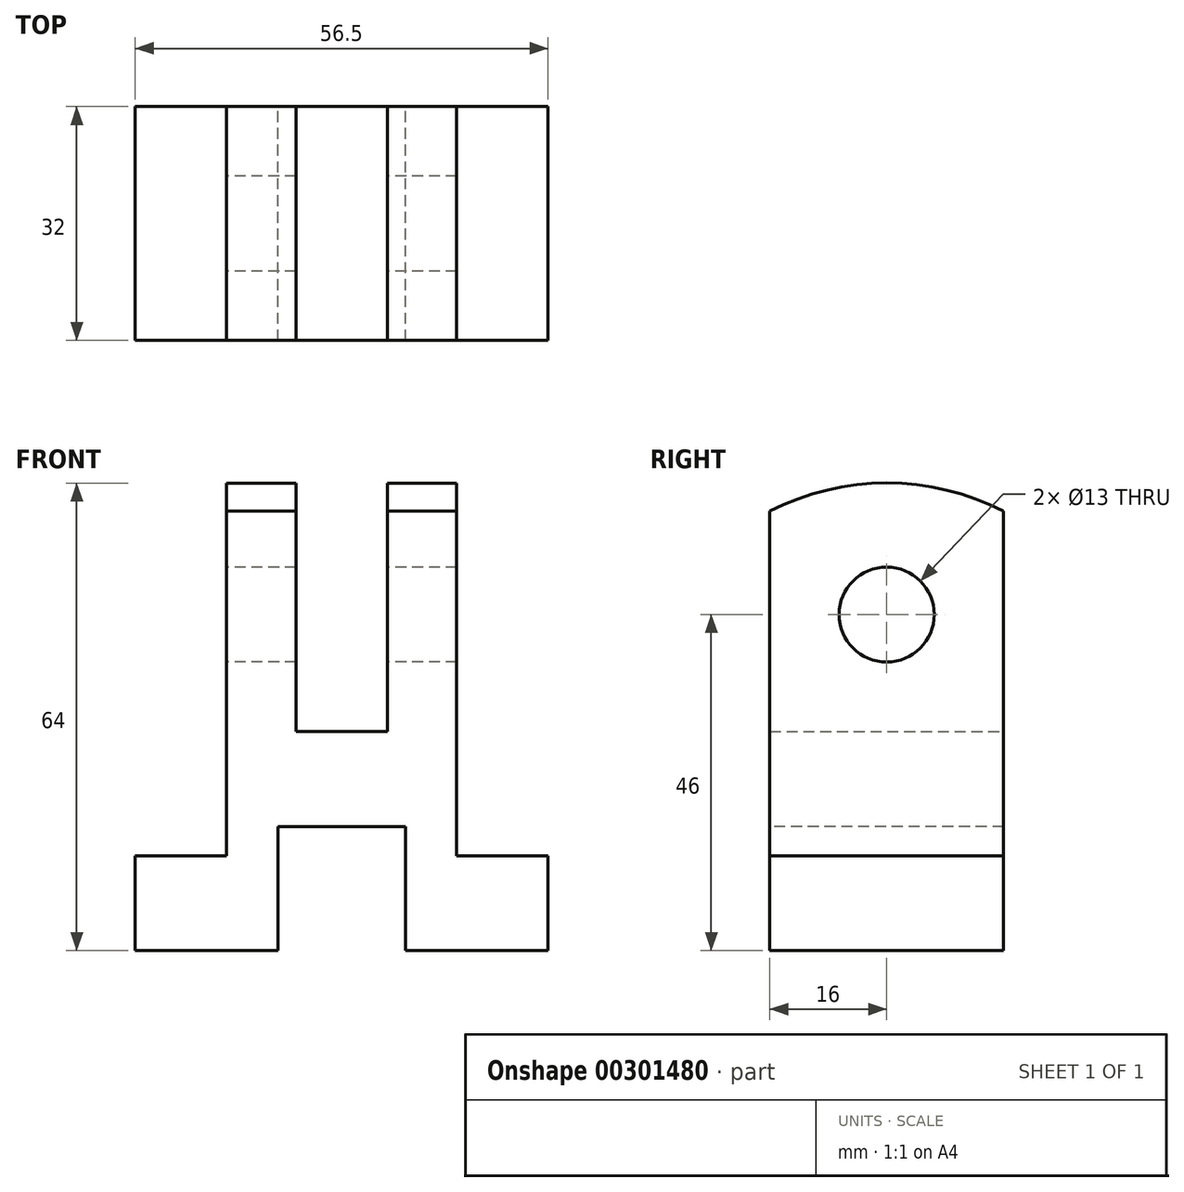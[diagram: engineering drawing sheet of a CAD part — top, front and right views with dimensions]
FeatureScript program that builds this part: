
annotation { "Feature Type Name" : "Feature", "Feature Type Description" : "" }
export const myFeature = defineFeature(function(context is Context, id is Id, definition is map)
    precondition{}
    {
        {
            var Q0;
            Q0=qCreatedBy(makeId("Right.planeOp"),FACE);
            var sketch = newSketch(context, id + "F0", { "sketchPlane" : qUnion([Q0])});
            skLineSegment(sketch, "E0", {"start": v(0, 0) * mm, "end": v(32, 0) * mm});
            skLineSegment(sketch, "E1", {"start": v(32, 0) * mm, "end": v(32, 60.13) * mm});
            skLineSegment(sketch, "E2", {"start": v(0, 60.13) * mm, "end": v(0, 0) * mm});
            skLineSegment(sketch, "E3", {"start": v(32, 17) * mm, "end": v(0, 17) * mm});
            skArc(sketch, "E4", {"start": v(32, 60.13) * mm, "mid": v(16, 64) * mm, "end": v(0, 60.13) * mm});
            skLineSegment(sketch, "E5", {"start": v(0, 13) * mm, "end": v(32, 13) * mm});
            skLineSegment(sketch, "E6", {"start": v(0, 30) * mm, "end": v(32, 30) * mm});
            skCircle(sketch, "E7", {"center": v(16, 46) * mm, "radius": 6.5 * mm});
            skSolve(sketch);
        }
        {
            var Q0;
            {var subQ0=sQuery(id+"F0.wireOp",EDGE,"E0");Q0=makeQuery(id+"F0.imprint","IMPRINT",FACE,{"disambiguationData":[TD([[makeQuery(id+"F0.imprint","IMPRINT",EDGE,{"derivedFrom":subQ0}),1.0]])]});}
            extrude(context, id + "F1", {"entities" : qUnion([Q0]), "endBound" : BoundingType.SYMMETRIC, "depth" : 56.5 * mm});
        }
        {
            var Q0;
            {var subQ0=sQuery(id+"F0.wireOp",EDGE,"E3");Q0=makeQuery(id+"F0.imprint","IMPRINT",FACE,{"disambiguationData":[TD([[makeQuery(id+"F0.imprint","IMPRINT",EDGE,{"derivedFrom":subQ0}),-1.0]])]});}
            var Q1;
            {var subQ0=sQuery(id+"F0.wireOp",EDGE,"E3");Q1=makeQuery(id+"F0.imprint","IMPRINT",FACE,{"disambiguationData":[TD([[makeQuery(id+"F0.imprint","IMPRINT",EDGE,{"derivedFrom":subQ0}),1.0]])]});}
            var Q2;
            {var subQ1=sQuery(id+"F0.wireOp",EDGE,"E4");Q2=makeQuery(id+"F0.imprint","IMPRINT",FACE,{"disambiguationData":[TD([[makeQuery(id+"F0.imprint","IMPRINT",EDGE,{"derivedFrom":subQ1}),1.0]])]});}
            extrude(context, id + "F2", {"entities" : qUnion([Q0, Q1, Q2]), "operationType" : NewBodyOperationType.ADD, "endBound" : BoundingType.SYMMETRIC, "depth" : 31.5 * mm});
        }
        {
            var Q0;
            {var subQ1=sQuery(id+"F0.wireOp",EDGE,"E4");Q0=makeQuery(id+"F0.imprint","IMPRINT",FACE,{"disambiguationData":[TD([[makeQuery(id+"F0.imprint","IMPRINT",EDGE,{"derivedFrom":subQ1}),1.0]])]});}
            extrude(context, id + "F3", {"entities" : qUnion([Q0]), "operationType" : NewBodyOperationType.REMOVE, "endBound" : BoundingType.SYMMETRIC, "depth" : 25 / 2 * mm});
        }
        {
            var Q0;
            {var subQ0=sQuery(id+"F0.wireOp",EDGE,"E3");Q0=makeQuery(id+"F0.imprint","IMPRINT",FACE,{"disambiguationData":[TD([[makeQuery(id+"F0.imprint","IMPRINT",EDGE,{"derivedFrom":subQ0}),1.0]])]});}
            var Q1;
            {var subQ0=sQuery(id+"F0.wireOp",EDGE,"E0");Q1=makeQuery(id+"F0.imprint","IMPRINT",FACE,{"disambiguationData":[TD([[makeQuery(id+"F0.imprint","IMPRINT",EDGE,{"derivedFrom":subQ0}),1.0]])]});}
            extrude(context, id + "F4", {"entities" : qUnion([Q0, Q1]), "operationType" : NewBodyOperationType.REMOVE, "endBound" : BoundingType.SYMMETRIC, "oppositeDirection" : true, "depth" : (35 / 2) * mm});
        }
        {
            var Q0;
            Q0=makeQuery(id+"F2.opExtrude","CAP_FACE",FACE,{"disambiguationData":[OSD([sQuery(id+"F0.wireOp",EDGE,"E1"),sQuery(id+"F0.wireOp",EDGE,"E2"),sQuery(id+"F0.wireOp",EDGE,"E4"),sQuery(id+"F0.wireOp",EDGE,"E5"),sQuery(id+"F0.wireOp",EDGE,"E7")])],"isStart":false});
            cPlane(context, id + "F5", {"entities" : qUnion([Q0]), "cplaneType" : CPlaneType.OFFSET, "offset" : 25 * mm, "width" : 150 * mm, "height" : 150 * mm});
        }
        {
            var Q0;
            Q0=qCreatedBy(id+"F5.planeOp",FACE);
            var sketch = newSketch(context, id + "F6", { "sketchPlane" : qUnion([Q0])});
            skCircle(sketch, "E8.0", {"center": v(16, 46) * mm, "radius": 6.5 * mm});
            skSolve(sketch);
        }
        {
            var Q0;
            Q0 = qSketchRegion(id + "F6", true);
            extrude(context, id + "F7", {"entities" : qUnion([Q0]), "depth" : 50 * mm});
        }
        {
            var Q0;
            Q0=makeQuery(id+"F7.opExtrude","SWEPT_BODY",BODY,{"disambiguationData":[OSD([sQuery(id+"F6.wireOp",EDGE,"E8.0")])]});
            deleteBodies(context, id + "F8", {"entities" : qUnion([Q0])});
        }
    });
